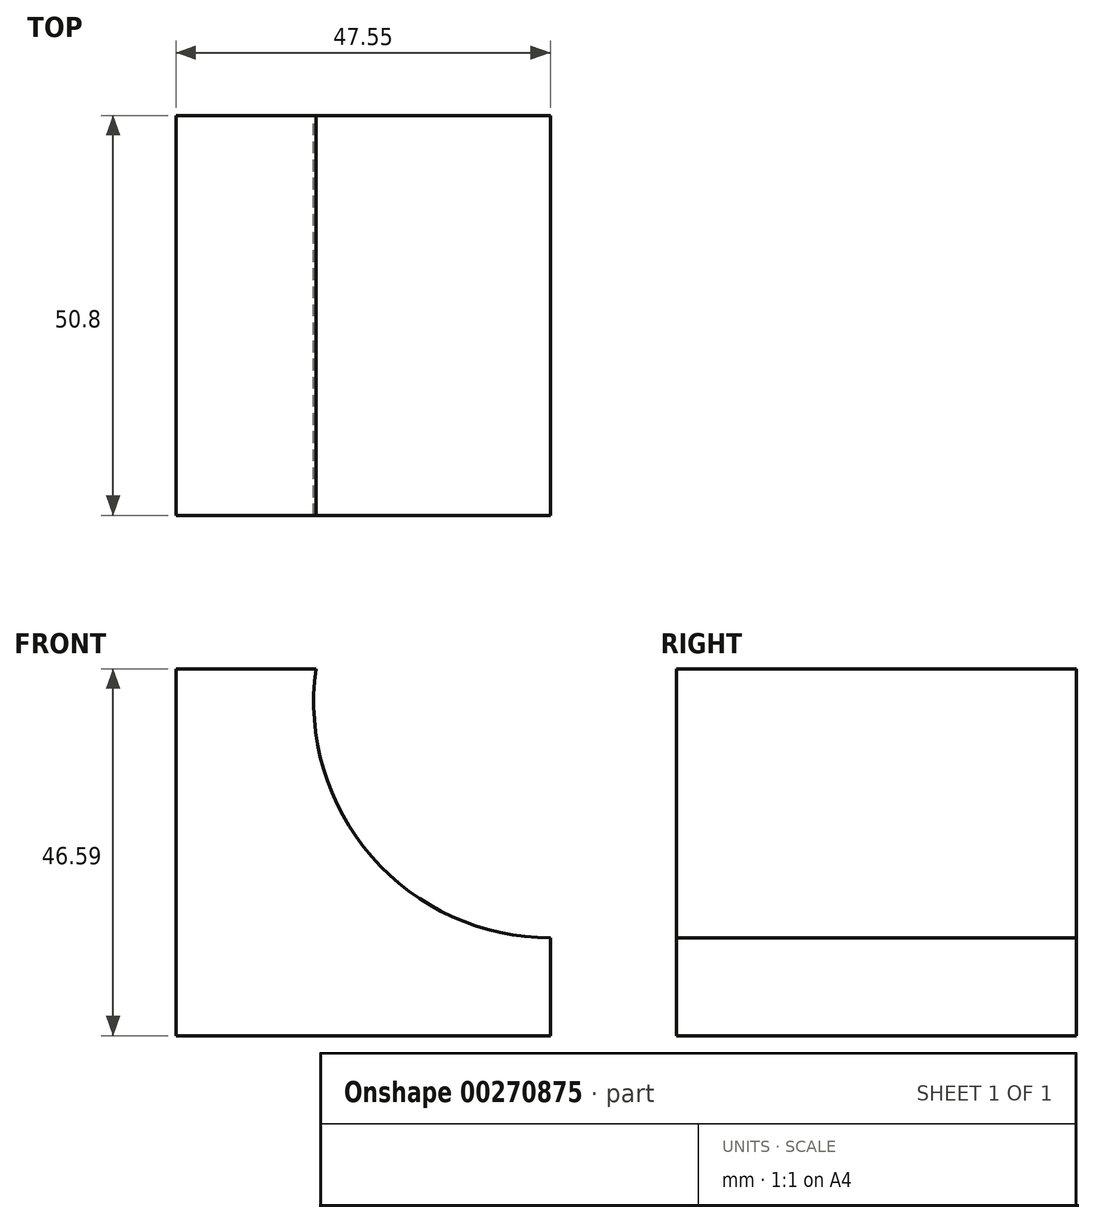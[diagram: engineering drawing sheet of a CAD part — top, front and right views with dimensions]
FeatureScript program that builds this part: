
annotation { "Feature Type Name" : "Feature", "Feature Type Description" : "" }
export const myFeature = defineFeature(function(context is Context, id is Id, definition is map)
    precondition{}
    {
        {
            var Q0;
            Q0=qCreatedBy(makeId("Front.planeOp"),FACE);
            var sketch = newSketch(context, id + "F0", { "sketchPlane" : qUnion([Q0])});
            skLineSegment(sketch, "E0.bottom", {"start": v(0, 0) * mm, "end": v(-47.55, 0) * mm});
            skLineSegment(sketch, "E0.top", {"start": v(0, 0) * mm, "end": v(-47.55, 0) * mm});
            skLineSegment(sketch, "E0.left", {"start": v(0, 0) * mm, "end": v(0, 0) * mm});
            skLineSegment(sketch, "E0.right", {"start": v(-47.55, 0) * mm, "end": v(-47.55, 0) * mm});
            skLineSegment(sketch, "E1.bottom", {"start": v(-47.55, 46.6) * mm, "end": v(-47.55, 46.6) * mm});
            skLineSegment(sketch, "E1.left", {"start": v(-47.55, 46.6) * mm, "end": v(-47.55, 0) * mm});
            skLineSegment(sketch, "E1.right", {"start": v(-47.55, 46.6) * mm, "end": v(-47.55, 0) * mm});
            skLineSegment(sketch, "E2.bottom", {"start": v(-47.55, 46.6) * mm, "end": v(-29.79, 46.6) * mm});
            skLineSegment(sketch, "E2.top", {"start": v(-47.55, 46.6) * mm, "end": v(-29.79, 46.6) * mm});
            skLineSegment(sketch, "E2.right", {"start": v(-29.79, 46.6) * mm, "end": v(-29.79, 46.6) * mm});
            skLineSegment(sketch, "E3.top", {"start": v(0, 12.41) * mm, "end": v(0, 12.41) * mm});
            skLineSegment(sketch, "E3.left", {"start": v(0, 0) * mm, "end": v(0, 12.41) * mm});
            skLineSegment(sketch, "E3.right", {"start": v(0, 0) * mm, "end": v(0, 12.41) * mm});
            skArc(sketch, "E4", {"start": v(-29.79, 46.6) * mm, "mid": v(-22.67, 22.73) * mm, "end": v(0, 12.41) * mm});
            skSolve(sketch);
        }
        {
            var Q0;
            Q0 = qSketchRegion(id + "F0", true);
            extrude(context, id + "F1", {"entities" : qUnion([Q0]), "depth" : 50.8 * mm});
        }
    });
